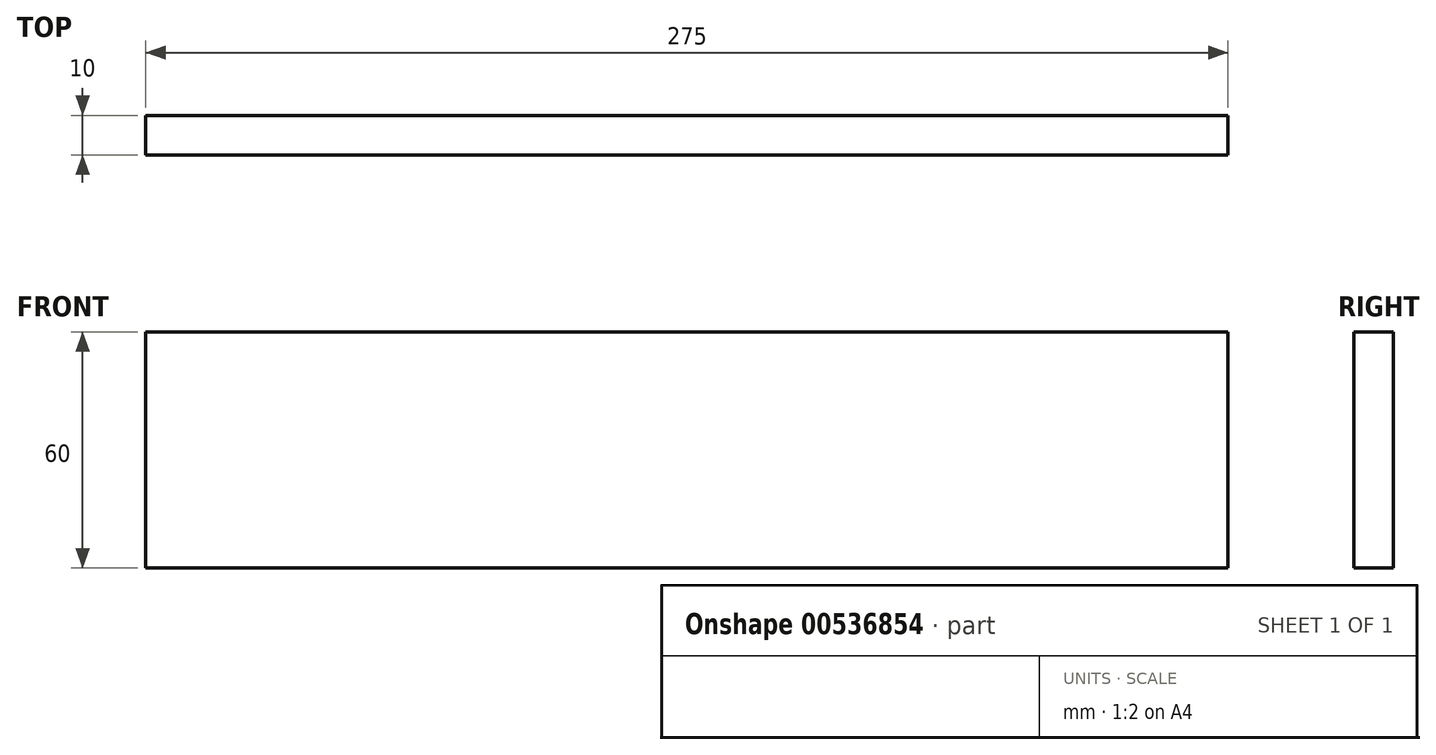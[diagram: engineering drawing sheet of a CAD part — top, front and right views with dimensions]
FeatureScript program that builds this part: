
annotation { "Feature Type Name" : "Feature", "Feature Type Description" : "" }
export const myFeature = defineFeature(function(context is Context, id is Id, definition is map)
    precondition{}
    {
        {
            var Q0;
            Q0=qCreatedBy(makeId("Front.planeOp"),FACE);
            var sketch = newSketch(context, id + "F0", { "sketchPlane" : qUnion([Q0])});
            skLineSegment(sketch, "E0.bottom", {"start": v(137.5, -30) * mm, "end": v(-137.5, -30) * mm});
            skLineSegment(sketch, "E0.top", {"start": v(137.5, 30) * mm, "end": v(-137.5, 30) * mm});
            skLineSegment(sketch, "E0.left", {"start": v(137.5, -30) * mm, "end": v(137.5, 30) * mm});
            skLineSegment(sketch, "E0.right", {"start": v(-137.5, -30) * mm, "end": v(-137.5, 30) * mm});
            skPoint(sketch, "E0.middle", {"position": v(0, 0) * mm});
            skSolve(sketch);
        }
        {
            var Q0;
            Q0=qSketchRegion(id+"F0",true);
            extrude(context, id + "F1", {"entities" : qUnion([Q0]), "endBound" : BoundingType.SYMMETRIC, "depth" : 10 * mm, "offsetDistance" : 25 * mm});
        }
    });
